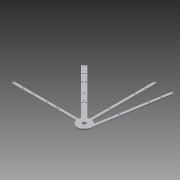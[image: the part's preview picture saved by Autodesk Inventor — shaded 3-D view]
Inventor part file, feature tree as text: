
AUTODESK INVENTOR PART (.ipt)
format: ipt  version: 2013 (Build 170138000, 138)  size: 229,376 bytes
history: native  units: in
note: dims shown in document units (in); Inventor stores cm internally (conversion verified against a paired STEP export)
features: extrude x3, sketch x3
ambient origin geometry x8: Origin, YZ Plane, XZ Plane, XY Plane, X Axis, Y Axis, Z Axis, Center Point
feature tree (6):
  extrude  "Extrusion2"  Depth=1.5in
  extrude  "Extrusion8"  Depth=0.25in
  extrude  "Extrusion9"  Depth=2.1762in
  sketch  "Sketch1"  dims[d0=0.5in d1=4.0in d2=0.5in d3=0.5in d4=1.5in d5=1.5in d6=1.5in d7=0.25in d8=0.25in d9=0.25in d10=0.5in d11=0.5in d12=3.75in d14=0.266in d15=0.266in d16=0.266in d17=0.25in d18=0.266in d19=0.25in d20=0.25in d21=0.266in d22=0.266in d23=0.266in d24=0.25in d25=0.25in d26=0.266in d28=1.125in d30=0.266in d32=0.266in d33=0.25in d36=1.5in]
  sketch  "Sketch6"  dims[d37=1.0in d38=0.25in]
  sketch  "Sketch8"  dims[d39=5.5in d40=2.1762in d41=5.5in d42=0.25in d43=0.25in d44=0.2874in d45=10.926in d46=10.6389in d47=0.2871in d48=0.2871in d49=15.5in d50=15.5in d51=0.25in d52=0.5in d53=0.266in d54=0.25in d55=0.266in d56=0.266in d57=15.5in d58=0.25in d60=0.266in d61=0.25in d62=0.266in d63=0.266in d64=0.266in d65=0.266in d66=2.0in d67=2.0in d68=2.0in d71=0.297in d72=0.297in d73=0.297in d74=0.297in d75=2.0in d77=0.0in d78=0.25in d79=0.25in d80=0.0in d115=0.266in d117=0.266in d118=9.75in d122=6.0in d123=8.0in d124=0.266in d126=6.0in d127=8.0in d129=0.25in d130=0.25in d131=0.25in d132=0.25in d133=1.0in d134=0.0in d135=0.748in d136=0.25in d137=0.0in]
